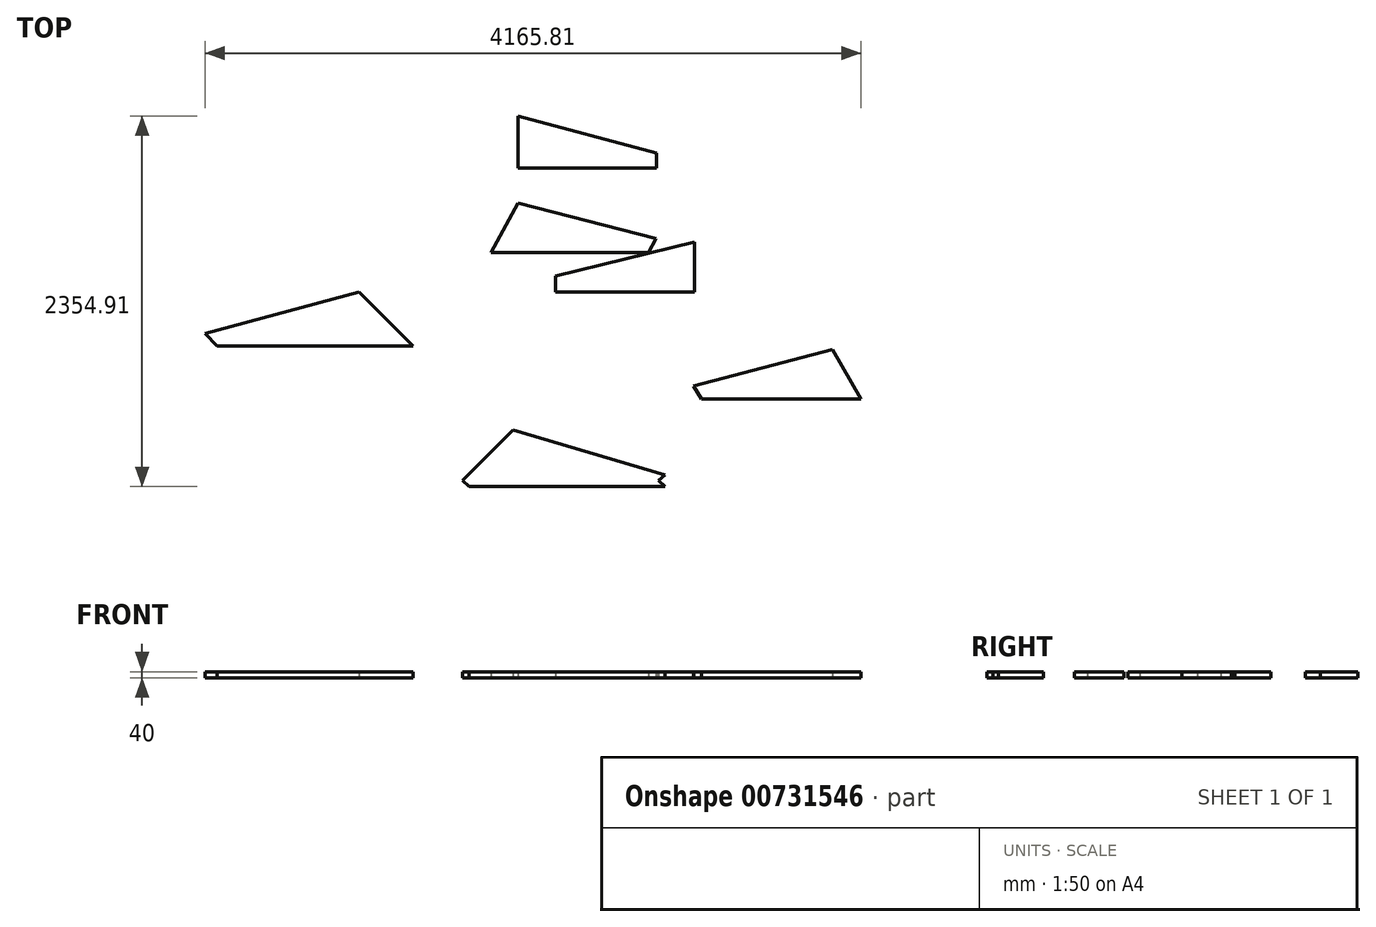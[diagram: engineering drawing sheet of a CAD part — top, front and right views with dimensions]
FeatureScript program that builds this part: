
annotation { "Feature Type Name" : "Feature", "Feature Type Description" : "" }
export const myFeature = defineFeature(function(context is Context, id is Id, definition is map)
    precondition{}
    {
        {
            var Q0;
            Q0=qCreatedBy(makeId("Top.planeOp"),FACE);
            var sketch = newSketch(context, id + "F0", { "sketchPlane" : qUnion([Q0])});
            skLineSegment(sketch, "E0", {"start": v(-522.03, -214.15) * mm, "end": v(-522.03, -315.15) * mm});
            skLineSegment(sketch, "E1", {"start": v(-522.03, -315.15) * mm, "end": v(357.97, -315.15) * mm});
            skLineSegment(sketch, "E2", {"start": v(357.97, -315.15) * mm, "end": v(357.97, 1.85) * mm});
            skLineSegment(sketch, "E3", {"start": v(357.97, 1.85) * mm, "end": v(-522.03, -214.15) * mm});
            skLineSegment(sketch, "E4", {"start": v(-469.65, -574.53) * mm, "end": v(420.82, -574.53) * mm});
            skSolve(sketch);
        }
        {
            var Q0;
            Q0=makeQuery(id+"F0.imprint","IMPRINT",FACE,{"disambiguationData":[TD([[makeQuery(id+"F0.imprint","IMPRINT",EDGE,{"derivedFrom":sQuery(id+"F0.wireOp",EDGE,"E0")}),1.0]])]});
            extrude(context, id + "F1", {"entities" : qUnion([Q0]), "depth" : 40 * mm, "offsetDistance" : 25 * mm});
        }
        {
            var Q0;
            Q0=qCreatedBy(makeId("Top.planeOp"),FACE);
            var sketch = newSketch(context, id + "F2", { "sketchPlane" : qUnion([Q0])});
            skLineSegment(sketch, "E5", {"start": v(-932.6, -66.5) * mm, "end": v(67.4, -66.5) * mm});
            skLineSegment(sketch, "E6", {"start": v(67.4, -66.5) * mm, "end": v(115.4, 23.5) * mm});
            skLineSegment(sketch, "E7", {"start": v(-761.6, 250.5) * mm, "end": v(-932.6, -66.5) * mm});
            skLineSegment(sketch, "E8", {"start": v(-761.6, 250.5) * mm, "end": v(115.4, 23.5) * mm});
            skSolve(sketch);
        }
        {
            var Q0;
            Q0 = qSketchRegion(id + "F2", true);
            extrude(context, id + "F3", {"entities" : qUnion([Q0]), "depth" : 25 * mm, "offsetDistance" : 25 * mm});
        }
        {
            var Q0;
            Q0 = qSketchRegion(id + "F2", true);
            extrude(context, id + "F4", {"entities" : qUnion([Q0]), "operationType" : NewBodyOperationType.ADD, "depth" : 40 * mm, "offsetDistance" : 25 * mm});
        }
        {
            var Q0;
            Q0=qCreatedBy(makeId("Top.planeOp"),FACE);
            var sketch = newSketch(context, id + "F5", { "sketchPlane" : qUnion([Q0])});
            skLineSegment(sketch, "E9", {"start": v(-793, -1192.63) * mm, "end": v(171, -1479.63) * mm});
            skLineSegment(sketch, "E10", {"start": v(171, -1479.63) * mm, "end": v(132, -1512.63) * mm});
            skLineSegment(sketch, "E11", {"start": v(132, -1512.63) * mm, "end": v(171, -1552.63) * mm});
            skLineSegment(sketch, "E12", {"start": v(171, -1552.63) * mm, "end": v(-1074, -1552.63) * mm});
            skLineSegment(sketch, "E13", {"start": v(-1074, -1552.63) * mm, "end": v(-1113, -1512.63) * mm});
            skLineSegment(sketch, "E14", {"start": v(-1113, -1512.63) * mm, "end": v(-793, -1192.63) * mm});
            skSolve(sketch);
        }
        {
            var Q0;
            Q0 = qSketchRegion(id + "F5", true);
            extrude(context, id + "F6", {"entities" : qUnion([Q0]), "depth" : 40 * mm, "offsetDistance" : 25 * mm});
        }
        {
            var Q0;
            Q0=qCreatedBy(makeId("Top.planeOp"),FACE);
            var sketch = newSketch(context, id + "F7", { "sketchPlane" : qUnion([Q0])});
            skLineSegment(sketch, "E15", {"start": v(-2749.36, -580.74) * mm, "end": v(-2672.36, -657.74) * mm});
            skLineSegment(sketch, "E16", {"start": v(-2672.36, -657.74) * mm, "end": v(-1427.36, -657.74) * mm});
            skLineSegment(sketch, "E17", {"start": v(-1427.36, -657.74) * mm, "end": v(-1770.36, -314.74) * mm});
            skLineSegment(sketch, "E18", {"start": v(-1770.36, -314.74) * mm, "end": v(-2749.36, -580.74) * mm});
            skSolve(sketch);
        }
        {
            var Q0;
            Q0 = qSketchRegion(id + "F7", true);
            extrude(context, id + "F8", {"entities" : qUnion([Q0]), "depth" : 40 * mm, "offsetDistance" : 25 * mm});
        }
        {
            var Q0;
            Q0=qCreatedBy(makeId("Top.planeOp"),FACE);
            var sketch = newSketch(context, id + "F9", { "sketchPlane" : qUnion([Q0])});
            skLineSegment(sketch, "E19", {"start": v(354.45, -912.75) * mm, "end": v(402.45, -996.75) * mm});
            skLineSegment(sketch, "E20", {"start": v(402.45, -996.75) * mm, "end": v(1416.45, -996.75) * mm});
            skLineSegment(sketch, "E21", {"start": v(1416.45, -996.75) * mm, "end": v(1235.45, -680.75) * mm});
            skLineSegment(sketch, "E22", {"start": v(1235.45, -680.75) * mm, "end": v(354.45, -912.75) * mm});
            skSolve(sketch);
        }
        {
            var Q0;
            Q0 = qSketchRegion(id + "F9", true);
            extrude(context, id + "F10", {"entities" : qUnion([Q0]), "depth" : 40 * mm, "offsetDistance" : 25 * mm});
        }
        {
            var Q0;
            Q0=qCreatedBy(makeId("Top.planeOp"),FACE);
            var sketch = newSketch(context, id + "F11", { "sketchPlane" : qUnion([Q0])});
            skLineSegment(sketch, "E23", {"start": v(-761.88, 802.28) * mm, "end": v(-761.88, 471.28) * mm});
            skLineSegment(sketch, "E24", {"start": v(-761.88, 471.28) * mm, "end": v(118.12, 471.28) * mm});
            skLineSegment(sketch, "E25", {"start": v(118.12, 471.28) * mm, "end": v(118.12, 565.28) * mm});
            skLineSegment(sketch, "E26", {"start": v(118.12, 565.28) * mm, "end": v(-761.88, 802.28) * mm});
            skSolve(sketch);
        }
        {
            var Q0;
            Q0 = qSketchRegion(id + "F11", true);
            extrude(context, id + "F12", {"entities" : qUnion([Q0]), "depth" : 40 * mm, "offsetDistance" : 25 * mm});
        }
    });
